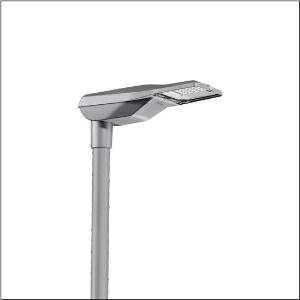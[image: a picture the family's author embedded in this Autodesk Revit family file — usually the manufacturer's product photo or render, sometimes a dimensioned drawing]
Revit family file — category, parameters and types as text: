
# Revit family: streetlight_sl_21_micro___stw1_0a_5xe5e33a08db_7e19
name_source: partatom
category: Lighting Fixtures
units: mm (PartAtom-declared; Revit-internal decimal feet)

## family parameters
Cut with Voids When Loaded = No
Host = Face
Light Source = No
Part Type = Normal
Room Calculation Point = No
Round Connector Dimension = Use Diameter
Shared = No

## types (1)
- --- (1 x LED, 5110 lm, 39.1 W, 3000K)
    Apparent Load = 39 VA
    CIE Flux Codes = 38 75 98 100 100
    Color Rendering = 70
    Color Temperature = 3000K
    Default Elevation = 1800 mm
    Description = Streetlight SL 21 micro, mast luminaire, primary light control with lens, of PMMA, primary optical cover: cover, of toughened safety glass, transparent, light distribution: STW1.0a, light emission: direct distribution, primary light characteristic: asymmetric, installation type: side-entry, post-top, LED, 3G 1.5mm², High Power LED, rated luminous flux: 5.110lm, luminous efficacy: 131lm/W, light colour: 730, colour temperature: 3000K, control: flexible luminous flux parameterisation, time-dependent luminous flux control, constant luminous flux control, overheat protection, mains connection: 230..240V, AC, 50/60Hz, connection cable pre-assembled, cable length: 6,5m, wiring characteristics: H07RN-F, start of lifetime: 39W, end of service life: 41W, reduction: 18W, luminaire housing, of diecast aluminium, powder-coated, Siteco® metallic grey (DB 702S), corrosivity category C5 mid according to DIN EN ISO 12944, please order mast flange separately, inclination adjustable: 0°, 5°, 10°, 15°, sealing non-destructively replaceable, multi-level sealing system, length: 528mm, width: 235mm, height: 110mm, mast flange for spigot size: 42mm (side-entry): 5XC10008XM4, 60/48mm (side-entry/post-top): 5XC10108XM2, 76/60mm (side-entry/post-top): 5XC10108XM1, protection rating (complete): IP66, insulation class (complete): insulation class II (safety insulation), certification: CE, ENEC, ENEC+, VDE, impact resistance: IK09, permissible operating ambient temperature for outdoor applications: -40..+50°C, standard-compliant lighting for roads and squares, packaging unit: 1 piece

Light Distribution: STW1.0a
    Height = 110 mm
    Lamp = 1 x LED
    Lamp Light Flux = 5110 lm
    Lamp Power = 39.1 W
    Lamp count = 1
    Length = 528 mm
    Luminous efficacy = 131 lm/W
    Manufacturer = Siteco
    ModVariant = No
    Model = 5XE5E33A08DB
    Number of Poles = 1
    OnlyDefault = Yes
    Power Factor = 1
    Product Name = Streetlight SL 21 micro | STW1.0a
    Product group = mast luminaire | pylon top
    ProductGroupID = 6100
    Protection Class = Protection class II
    Protection Degree = IP 66
    RLX_Detail_Level = 1
    RLX_Emergency_Light_Flux = 0 lm
    RLX_Emergency_Type = 0
    RLX_Emergency_Type_DB = No
    RlxData = <blob elided: 99529 chars, md5=0c9b5982>
    Socket = socket
    Standby Power = 0 W
    System Light Flux = 5110 lm
    System Power = 39 W
    Type Comments = factory setting: luminous flux: 100 % | Output Level: 100 % | 765 mA
    Type Image = l_1006881.jpg
    URL = http://relux.com
    VarID = @adj_087445
    Voltage = 0 V
    Weight = 0.00 kg
    Width = 235 mm

## geometry (parser evidence)
native form markers: Blend x4, Sweep x9
no freeform markers — native parametric forms only
